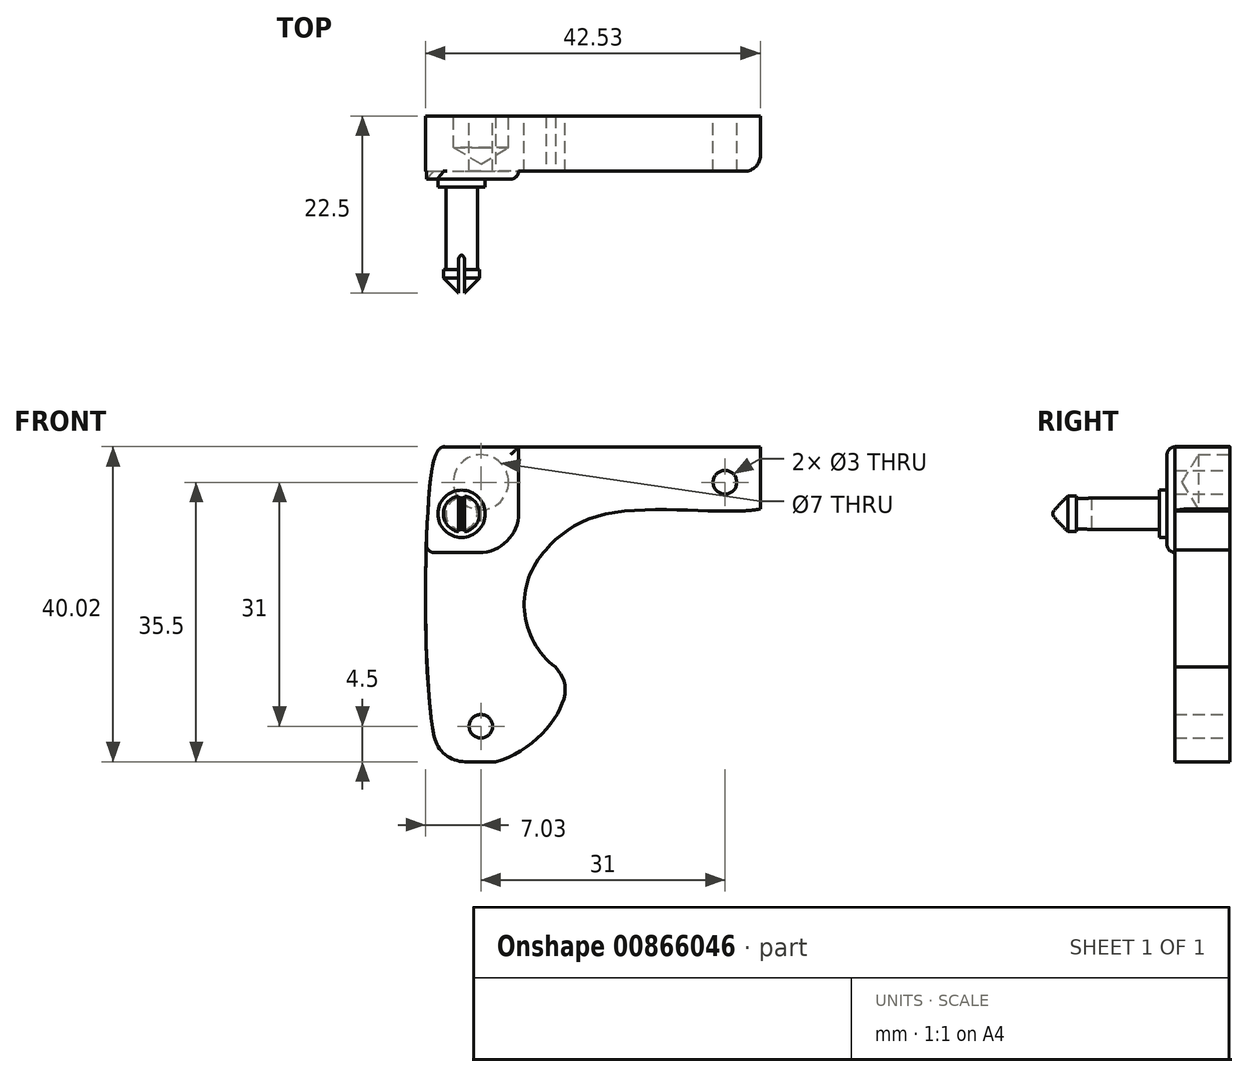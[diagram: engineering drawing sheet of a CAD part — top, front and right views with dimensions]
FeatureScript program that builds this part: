
annotation { "Feature Type Name" : "Feature", "Feature Type Description" : "" }
export const myFeature = defineFeature(function(context is Context, id is Id, definition is map)
    precondition{}
    {
        {
            var Q0;
            Q0=qCreatedBy(makeId("Front.planeOp"),FACE);
            var sketch = newSketch(context, id + "F0", { "sketchPlane" : qUnion([Q0])});
            skLineSegment(sketch, "E0.bottom", {"start": v(-20, 20) * mm, "end": v(20, 20) * mm});
            skLineSegment(sketch, "E0.top", {"start": v(-20, -20) * mm, "end": v(20, -20) * mm});
            skLineSegment(sketch, "E0.left", {"start": v(-20, 20) * mm, "end": v(-20, -20) * mm});
            skLineSegment(sketch, "E0.right", {"start": v(20, 20) * mm, "end": v(20, -20) * mm});
            skPoint(sketch, "E1", {"position": v(-15.5, 15.5) * mm});
            skPoint(sketch, "E2", {"position": v(15.5, 15.5) * mm});
            skPoint(sketch, "E3", {"position": v(15.5, -15.5) * mm});
            skPoint(sketch, "E4", {"position": v(-15.5, -15.5) * mm});
            skPoint(sketch, "E5", {"position": v(0, 0) * mm});
            skFitSpline(sketch, "E6", {"points": [v(-20, 20) * mm, v(-22.22, 12.2) * mm, v(-20, -20) * mm, v(-13.87, 3.79) * mm, v(-20, 20) * mm]});
            skSolve(sketch);
        }
        {
            var Q0;
            Q0=makeQuery(id+"F0.imprint","IMPRINT",FACE,{"disambiguationData":[TD([[makeQuery(id+"F0.imprint","IMPRINT",EDGE,{"derivedFrom":sQuery(id+"F0.wireOp",EDGE,"E0.bottom")}),-1.0]])]});
            var Q1;
            {var subQ1=sQuery(id+"F0.wireOp",EDGE,"E0.left");Q1=makeQuery(id+"F0.imprint","IMPRINT",FACE,{"disambiguationData":[TD([[makeQuery(id+"F0.imprint","IMPRINT",EDGE,{"derivedFrom":subQ1}),1.0]])]});}
            var Q2;
            {var subQ0=sQuery(id+"F0.wireOp",EDGE,"E0.left");Q2=makeQuery(id+"F0.imprint","IMPRINT",FACE,{"disambiguationData":[TD([[makeQuery(id+"F0.imprint","IMPRINT",EDGE,{"derivedFrom":subQ0}),-1.0]])]});}
            extrude(context, id + "F1", {"entities" : qUnion([Q0, Q1, Q2]), "depth" : 7 * mm, "offsetDistance" : 25 * mm});
        }
        {
            var Q0;
            Q0=sQuery(id+"F0.wireOp",VERTEX,"E5");
            var Q1;
            Q1=makeQuery(id+"F1.opExtrude","SWEPT_BODY",BODY,{"disambiguationData":[OSD([sQuery(id+"F0.wireOp",EDGE,"E0.bottom"),sQuery(id+"F0.wireOp",EDGE,"E0.top"),sQuery(id+"F0.wireOp",EDGE,"E0.left"),sQuery(id+"F0.wireOp",EDGE,"E0.right")])]});
            hole(context, id + "F2", {"style" : HoleStyle.SIMPLE, "endStyle" : HoleEndStyle.THROUGH, "oppositeDirection" : true, "holeDiameter" : 20 * mm, "majorDiameter" : 5 * mm, "isTappedThrough" : true, "tappedDepth" : 12 * mm, "tapClearance" : 3, "locations" : qUnion([Q0]), "scope" : qUnion([Q1])});
        }
        {
            var Q0;
            Q0=sQuery(id+"F0.wireOp",VERTEX,"E2");
            var Q1;
            Q1=sQuery(id+"F0.wireOp",VERTEX,"E3");
            var Q2;
            Q2=sQuery(id+"F0.wireOp",VERTEX,"E4");
            var Q3;
            Q3=makeQuery(id+"F1.opExtrude","SWEPT_BODY",BODY,{"disambiguationData":[OSD([sQuery(id+"F0.wireOp",EDGE,"E0.bottom"),sQuery(id+"F0.wireOp",EDGE,"E0.top"),sQuery(id+"F0.wireOp",EDGE,"E0.left"),sQuery(id+"F0.wireOp",EDGE,"E0.right")])]});
            hole(context, id + "F3", {"style" : HoleStyle.SIMPLE, "endStyle" : HoleEndStyle.THROUGH, "oppositeDirection" : true, "holeDiameter" : 3 * mm, "majorDiameter" : 5 * mm, "isTappedThrough" : true, "tappedDepth" : 12 * mm, "tapClearance" : 3, "locations" : qUnion([Q0, Q1, Q2]), "scope" : qUnion([Q3])});
        }
        {
            var Q0;
            Q0=sQuery(id+"F0.wireOp",VERTEX,"E1");
            var Q1;
            Q1=makeQuery(id+"F1.opExtrude","SWEPT_BODY",BODY,{"disambiguationData":[OSD([sQuery(id+"F0.wireOp",EDGE,"E0.bottom"),sQuery(id+"F0.wireOp",EDGE,"E0.top"),sQuery(id+"F0.wireOp",EDGE,"E0.left"),sQuery(id+"F0.wireOp",EDGE,"E0.right")])]});
            hole(context, id + "F4", {"style" : HoleStyle.SIMPLE, "endStyle" : HoleEndStyle.BLIND, "oppositeDirection" : true, "holeDiameter" : 7 * mm, "majorDiameter" : 5 * mm, "holeDepth" : 4 * mm, "isTappedThrough" : true, "tappedDepth" : 12 * mm, "tapClearance" : 3, "locations" : qUnion([Q0]), "scope" : qUnion([Q1])});
        }
        {
            var Q0;
            Q0=qCreatedBy(makeId("Front.planeOp"),FACE);
            var sketch = newSketch(context, id + "F5", { "sketchPlane" : qUnion([Q0])});
            skLineSegment(sketch, "E7", {"start": v(0, 6.5) * mm, "end": v(-44.68, 6.5) * mm});
            skCircle(sketch, "E8", {"center": v(0, 0) * mm, "radius": 6.5 * mm});
            skSolve(sketch);
        }
        {
            var Q0;
            Q0=makeQuery(id+"F1.opExtrude","CAP_FACE",FACE,{"disambiguationData":[OSD([sQuery(id+"F0.wireOp",EDGE,"E0.bottom"),sQuery(id+"F0.wireOp",EDGE,"E0.top"),sQuery(id+"F0.wireOp",EDGE,"E0.left"),sQuery(id+"F0.wireOp",EDGE,"E0.right")])],"isStart":false});
            var sketch = newSketch(context, id + "F6", { "sketchPlane" : qUnion([Q0])});
            skLineSegment(sketch, "E9.bottom", {"start": v(-23.6, 20) * mm, "end": v(-10.72, 20) * mm});
            skLineSegment(sketch, "E9.top", {"start": v(-23.6, 6.57) * mm, "end": v(-10.72, 6.57) * mm});
            skLineSegment(sketch, "E9.left", {"start": v(-23.6, 20) * mm, "end": v(-23.6, 6.57) * mm});
            skLineSegment(sketch, "E9.right", {"start": v(-10.72, 20) * mm, "end": v(-10.72, 6.57) * mm});
            skSolve(sketch);
        }
        {
            var Q0;
            Q0=makeQuery(id+"F6.imprint","IMPRINT",FACE,{"disambiguationData":[TD([[makeQuery(id+"F6.imprint","IMPRINT",EDGE,{"derivedFrom":sQuery(id+"F6.wireOp",EDGE,"E9.bottom")}),-1.0]])]});
            extrude(context, id + "F7", {"entities" : qUnion([Q0]), "operationType" : NewBodyOperationType.ADD, "depth" : 1 * mm, "offsetDistance" : 25 * mm});
        }
        {
            var Q0;
            Q0=makeQuery(id+"F7.opExtrude","CAP_FACE",FACE,{"disambiguationData":[OSD([sQuery(id+"F6.wireOp",EDGE,"E9.bottom"),sQuery(id+"F6.wireOp",EDGE,"E9.top"),sQuery(id+"F6.wireOp",EDGE,"E9.left"),sQuery(id+"F6.wireOp",EDGE,"E9.right")])],"isStart":false});
            var sketch = newSketch(context, id + "F8", { "sketchPlane" : qUnion([Q0])});
            skCircle(sketch, "E10", {"center": v(-17.96, 11.5) * mm, "radius": 3 * mm});
            skSolve(sketch);
        }
        {
            var Q0;
            Q0=makeQuery(id+"F8.imprint","IMPRINT",FACE,{"disambiguationData":[TD([[makeQuery(id+"F8.imprint","IMPRINT",EDGE,{"derivedFrom":sQuery(id+"F8.wireOp",EDGE,"E10")}),1.0]])]});
            extrude(context, id + "F9", {"entities" : qUnion([Q0]), "operationType" : NewBodyOperationType.ADD, "depth" : 1 * mm, "offsetDistance" : 25 * mm});
        }
        {
            var Q0;
            Q0=makeQuery(id+"F9.opExtrude","CAP_FACE",FACE,{"disambiguationData":[OSD([sQuery(id+"F6.wireOp",EDGE,"E9.top"),sQuery(id+"F8.wireOp",EDGE,"E10")])],"isStart":false});
            var sketch = newSketch(context, id + "F10", { "sketchPlane" : qUnion([Q0])});
            skCircle(sketch, "E11", {"center": v(-17.96, 11.5) * mm, "radius": 2 * mm});
            skSolve(sketch);
        }
        {
            var Q0;
            Q0=makeQuery(id+"F10.imprint","IMPRINT",FACE,{"disambiguationData":[TD([[makeQuery(id+"F10.imprint","IMPRINT",EDGE,{"derivedFrom":sQuery(id+"F10.wireOp",EDGE,"E11")}),1.0]])]});
            extrude(context, id + "F11", {"entities" : qUnion([Q0]), "operationType" : NewBodyOperationType.ADD, "depth" : 10.5 * mm, "offsetDistance" : 25 * mm});
        }
        {
            var Q0;
            Q0=makeQuery(id+"F11.opExtrude","CAP_FACE",FACE,{"disambiguationData":[OSD([sQuery(id+"F10.wireOp",EDGE,"E11")])],"isStart":false});
            var sketch = newSketch(context, id + "F12", { "sketchPlane" : qUnion([Q0])});
            skCircle(sketch, "E12", {"center": v(-17.96, 11.5) * mm, "radius": 2.3 * mm});
            skSolve(sketch);
        }
        {
            var Q0;
            Q0=makeQuery(id+"F12.imprint","IMPRINT",FACE,{"disambiguationData":[TD([[makeQuery(id+"F12.imprint","IMPRINT",EDGE,{"derivedFrom":makeQuery(id+"F11.opExtrude","CAP_EDGE",EDGE,{"disambiguationData":[OSD([sQuery(id+"F10.wireOp",EDGE,"E11")])],"isStart":false})}),1.0]])]});
            var Q1;
            Q1=makeQuery(id+"F12.imprint","IMPRINT",FACE,{"disambiguationData":[TD([[makeQuery(id+"F12.imprint","IMPRINT",EDGE,{"derivedFrom":sQuery(id+"F12.wireOp",EDGE,"E12")}),1.0]])]});
            extrude(context, id + "F13", {"entities" : qUnion([Q0, Q1]), "operationType" : NewBodyOperationType.ADD, "depth" : 3 * mm, "offsetDistance" : 25 * mm});
        }
        {
            var Q0;
            Q0=makeQuery(id+"F13.opExtrude","CAP_FACE",FACE,{"disambiguationData":[OSD([sQuery(id+"F12.wireOp",EDGE,"E12")])],"isStart":false});
            var sketch = newSketch(context, id + "F14", { "sketchPlane" : qUnion([Q0])});
            skLineSegment(sketch, "E13.bottom", {"start": v(-17.56, 9.13) * mm, "end": v(-18.36, 9.13) * mm});
            skLineSegment(sketch, "E13.top", {"start": v(-17.56, 13.87) * mm, "end": v(-18.36, 13.87) * mm});
            skLineSegment(sketch, "E13.left", {"start": v(-17.56, 9.13) * mm, "end": v(-17.56, 13.87) * mm});
            skLineSegment(sketch, "E13.right", {"start": v(-18.36, 9.13) * mm, "end": v(-18.36, 13.87) * mm});
            skPoint(sketch, "E13.middle", {"position": v(-17.96, 11.5) * mm});
            skSolve(sketch);
        }
        {
            var Q0;
            {var subQ0=sQuery(id+"F14.wireOp",EDGE,"E13.top");Q0=makeQuery(id+"F14.imprint","IMPRINT",FACE,{"disambiguationData":[TD([[makeQuery(id+"F14.imprint","IMPRINT",EDGE,{"derivedFrom":subQ0}),1.0]])]});}
            var Q1;
            {var subQ0=sQuery(id+"F14.wireOp",EDGE,"E13.left");var subQ1=makeQuery(id+"F13.opExtrude","CAP_EDGE",EDGE,{"disambiguationData":[OSD([sQuery(id+"F12.wireOp",EDGE,"E12")])],"isStart":false});var subQ2=makeQuery(id+"F14.imprint","INTERSECT",VERTEX,{"disambiguationData":[OD(0.0)],"derivedFrom":[subQ1,subQ0]});Q1=makeQuery(id+"F14.imprint","IMPRINT",FACE,{"disambiguationData":[TD([[makeQuery(id+"F14.imprint","IMPRINT",EDGE,{"disambiguationData":[TD([[subQ2,-1.0]])],"derivedFrom":subQ0}),1.0]])]});}
            var Q2;
            {var subQ0=sQuery(id+"F14.wireOp",EDGE,"E13.bottom");Q2=makeQuery(id+"F14.imprint","IMPRINT",FACE,{"disambiguationData":[TD([[makeQuery(id+"F14.imprint","IMPRINT",EDGE,{"derivedFrom":subQ0}),-1.0]])]});}
            extrude(context, id + "F15", {"entities" : qUnion([Q0, Q1, Q2]), "operationType" : NewBodyOperationType.REMOVE, "oppositeDirection" : true, "depth" : 5 * mm, "offsetDistance" : 25 * mm});
        }
        {
            var Q0;
            {var subQ0=sQuery(id+"F12.wireOp",EDGE,"E12");Q0=makeQuery(id+"F15.boolean.opBoolean","SPLIT",EDGE,{"disambiguationData":[TD([makeQuery(id+"F15.opExtrude","SWEPT_FACE",FACE,{"disambiguationData":[OSD([sQuery(id+"F14.wireOp",EDGE,"E13.right")])]})])],"derivedFrom":makeQuery(id+"F13.opExtrude","CAP_EDGE",EDGE,{"disambiguationData":[OSD([subQ0])],"isStart":false})});}
            var Q1;
            {var subQ0=sQuery(id+"F12.wireOp",EDGE,"E12");Q1=makeQuery(id+"F15.boolean.opBoolean","SPLIT",EDGE,{"disambiguationData":[TD([makeQuery(id+"F15.opExtrude","SWEPT_FACE",FACE,{"disambiguationData":[OSD([sQuery(id+"F14.wireOp",EDGE,"E13.left")])]})])],"derivedFrom":makeQuery(id+"F13.opExtrude","CAP_EDGE",EDGE,{"disambiguationData":[OSD([subQ0])],"isStart":false})});}
            chamfer(context, id + "F16", {"entities" : qUnion([Q0, Q1]), "width" : 1.9 * mm, "tangentPropagation" : true});
        }
        {
            var Q0;
            {var subQ7=sQuery(id+"F6.wireOp",EDGE,"E9.top");Q0=makeQuery(id+"F6.imprint","IMPRINT",FACE,{"disambiguationData":[TD([[makeQuery(id+"F6.imprint","IMPRINT",EDGE,{"derivedFrom":subQ7}),-1.0]])]});}
            var sketch = newSketch(context, id + "F17", { "sketchPlane" : qUnion([Q0])});
            skFitSpline(sketch, "E14", {"points": [v(22.15, 16.76) * mm, v(21.52, 12.68) * mm, v(0, 11.37) * mm, v(-9.58, 2.55) * mm, v(-8.96, -4.93) * mm, v(-4.8, -10.46) * mm, v(-13.92, -20.06) * mm, v(-22.03, -19.9) * mm, v(13.8, -32.16) * mm, v(31.86, -14) * mm, v(30.6, 5.78) * mm, v(27.78, 17.76) * mm, v(23.51, 20.4) * mm, v(21.16, 19.76) * mm, v(22.15, 16.76) * mm]});
            skSolve(sketch);
        }
        {
            var Q0;
            {var subQ0=sQuery(id+"F17.wireOp",EDGE,"E14");var subQ1=makeQuery(id+"F6.imprint","IMPRINT",EDGE,{"derivedFrom":makeQuery(id+"F1.opExtrude","CAP_EDGE",EDGE,{"disambiguationData":[OSD([sQuery(id+"F0.wireOp",EDGE,"E0.right")])],"isStart":false})});var subQ2=makeQuery(id+"F17.imprint","INTERSECT",VERTEX,{"derivedFrom":[subQ1,subQ0]});Q0=makeQuery(id+"F17.imprint","IMPRINT",FACE,{"disambiguationData":[TD([[makeQuery(id+"F17.imprint","IMPRINT",EDGE,{"disambiguationData":[TD([[subQ2,1.0]])],"derivedFrom":subQ0}),1.0]])]});}
            var Q1;
            {var subQ0=sQuery(id+"F0.wireOp",EDGE,"E0.right");var subQ1=sQuery(id+"F0.wireOp",EDGE,"E0.top");var subQ3=makeQuery(id+"F6.imprint","IMPRINT",EDGE,{"derivedFrom":makeQuery(id+"F1.opExtrude","CAP_EDGE",EDGE,{"disambiguationData":[OSD([subQ0])],"isStart":false})});var subQ4=makeQuery(id+"F6.imprint","IMPRINT",EDGE,{"derivedFrom":makeQuery(id+"F1.opExtrude","CAP_EDGE",EDGE,{"disambiguationData":[OSD([subQ1])],"isStart":false})});var subQ5=makeQuery(id+"F17.imprint","INTERSECT",VERTEX,{"derivedFrom":[subQ4,subQ3]});Q1=makeQuery(id+"F17.imprint","IMPRINT",FACE,{"disambiguationData":[TD([[makeQuery(id+"F17.imprint","IMPRINT",EDGE,{"disambiguationData":[TD([[subQ5,1.0]])],"derivedFrom":subQ4}),1.0]])]});}
            extrude(context, id + "F18", {"entities" : qUnion([Q0, Q1]), "operationType" : NewBodyOperationType.REMOVE, "oppositeDirection" : true, "depth" : 25 * mm, "offsetDistance" : 25 * mm});
        }
        {
            var Q0;
            Q0=makeQuery(id+"F7.opExtrude","SWEPT_EDGE",EDGE,{"disambiguationData":[OSD([sQuery(id+"F6.wireOp",EDGE,"E9.top"),sQuery(id+"F6.wireOp",EDGE,"E9.right")])]});
            fillet(context, id + "F19", {"entities" : qUnion([Q0]), "radius" : 5 * mm, "tangentPropagation" : true, "allowEdgeOverflow" : false});
        }
        {
            var Q0;
            Q0=makeQuery(id+"F7.opExtrude","CAP_EDGE",EDGE,{"disambiguationData":[OSD([sQuery(id+"F6.wireOp",EDGE,"E9.top")])],"isStart":false});
            var Q1;
            {var subQ0=sQuery(id+"F6.wireOp",EDGE,"E9.right");var subQ1=sQuery(id+"F6.wireOp",EDGE,"E9.top");Q1=makeQuery(id+"F19.opFillet","BLEND_EDGE",EDGE,{"blendedFrom":[makeQuery(id+"F7.opExtrude","SWEPT_EDGE",EDGE,{"disambiguationData":[OSD([subQ1,subQ0])]}),makeQuery(id+"F7.opExtrude","CAP_FACE",FACE,{"disambiguationData":[OSD([sQuery(id+"F0.wireOp",EDGE,"E0.bottom"),sQuery(id+"F0.wireOp",EDGE,"E0.top"),sQuery(id+"F0.wireOp",EDGE,"E0.left"),sQuery(id+"F0.wireOp",EDGE,"E0.right"),sQuery(id+"F3.hole-0.sketch.wireOp",EDGE,"core_line_2"),sQuery(id+"F6.wireOp",EDGE,"E9.bottom"),subQ1,sQuery(id+"F6.wireOp",EDGE,"E9.left"),subQ0])],"isStart":false})],"blendedInto":[makeQuery(id+"F7.opExtrude","CAP_FACE",FACE,{"disambiguationData":[OSD([sQuery(id+"F0.wireOp",EDGE,"E0.bottom"),sQuery(id+"F0.wireOp",EDGE,"E0.top"),sQuery(id+"F0.wireOp",EDGE,"E0.left"),sQuery(id+"F0.wireOp",EDGE,"E0.right"),sQuery(id+"F3.hole-0.sketch.wireOp",EDGE,"core_line_2"),sQuery(id+"F6.wireOp",EDGE,"E9.bottom"),subQ1,sQuery(id+"F6.wireOp",EDGE,"E9.left"),subQ0])],"isStart":false})]});}
            var Q2;
            Q2=makeQuery(id+"F7.opExtrude","CAP_EDGE",EDGE,{"disambiguationData":[OSD([sQuery(id+"F6.wireOp",EDGE,"E9.bottom")])],"isStart":false});
            var Q3;
            Q3=makeQuery(id+"F7.opExtrude","SWEPT_EDGE",EDGE,{"disambiguationData":[OSD([sQuery(id+"F0.wireOp",EDGE,"E6"),sQuery(id+"F6.wireOp",EDGE,"E9.top")])]});
            fillet(context, id + "F20", {"entities" : qUnion([Q0, Q1, Q2, Q3]), "radius" : 1 * mm, "tangentPropagation" : true, "allowEdgeOverflow" : false});
        }
        {
            var Q0;
            Q0=makeQuery(id+"F2.hole-0.boolean.opBoolean","INTERSECT",EDGE,{"derivedFrom":[makeQuery(id+"F1.opExtrude","CAP_FACE",FACE,{"disambiguationData":[OSD([sQuery(id+"F0.wireOp",EDGE,"E0.bottom"),sQuery(id+"F0.wireOp",EDGE,"E0.top"),sQuery(id+"F0.wireOp",EDGE,"E0.left"),sQuery(id+"F0.wireOp",EDGE,"E0.right")])],"isStart":false}),makeQuery(id+"F2.hole-0.opRevolve","SWEPT_FACE",FACE,{"disambiguationData":[OSD([sQuery(id+"F2.hole-0.sketch.wireOp",EDGE,"core_line_2")])]})]});
            var Q1;
            {var subQ0=sQuery(id+"F0.wireOp",EDGE,"E0.right");var subQ1=sQuery(id+"F17.wireOp",EDGE,"E14");Q1=makeQuery(id+"F18.boolean.opBoolean","COPY",EDGE,{"disambiguationData":[TD([makeQuery(id+"F1.opExtrude","SWEPT_FACE",FACE,{"disambiguationData":[OSD([subQ0])]})])],"derivedFrom":makeQuery(id+"F18.opExtrude","CAP_EDGE",EDGE,{"disambiguationData":[OSD([subQ1])],"isStart":true})});}
            var Q2;
            {var subQ0=sQuery(id+"F0.wireOp",EDGE,"E0.top");var subQ1=sQuery(id+"F17.wireOp",EDGE,"E14");Q2=makeQuery(id+"F18.boolean.opBoolean","COPY",EDGE,{"disambiguationData":[TD([makeQuery(id+"F1.opExtrude","SWEPT_FACE",FACE,{"disambiguationData":[OSD([subQ0])]})])],"derivedFrom":makeQuery(id+"F18.opExtrude","CAP_EDGE",EDGE,{"disambiguationData":[OSD([subQ1])],"isStart":true})});}
            var Q3;
            Q3=makeQuery(id+"F1.opExtrude","CAP_EDGE",EDGE,{"disambiguationData":[OSD([sQuery(id+"F0.wireOp",EDGE,"E0.right")])],"isStart":false});
            fillet(context, id + "F21", {"entities" : qUnion([Q0, Q1, Q2, Q3]), "radius" : 2 * mm, "tangentPropagation" : true, "allowEdgeOverflow" : false});
        }
        {
            var Q0;
            Q0=makeQuery(id+"F15.boolean.opBoolean","COPY",EDGE,{"derivedFrom":makeQuery(id+"F15.opExtrude","CAP_EDGE",EDGE,{"disambiguationData":[OSD([sQuery(id+"F14.wireOp",EDGE,"E13.right")])],"isStart":false})});
            var Q1;
            Q1=makeQuery(id+"F15.boolean.opBoolean","COPY",EDGE,{"derivedFrom":makeQuery(id+"F15.opExtrude","CAP_EDGE",EDGE,{"disambiguationData":[OSD([sQuery(id+"F14.wireOp",EDGE,"E13.left")])],"isStart":false})});
            fillet(context, id + "F22", {"entities" : qUnion([Q0, Q1]), "radius" : 0.8 * mm, "tangentPropagation" : true, "allowEdgeOverflow" : false});
        }
        {
            var Q0;
            Q0=makeQuery(id+"F7.boolean.opBoolean","MERGE",EDGE,{"derivedFrom":[makeQuery(id+"F1.opExtrude","SWEPT_EDGE",EDGE,{"disambiguationData":[OSD([sQuery(id+"F0.wireOp",EDGE,"E0.bottom"),sQuery(id+"F0.wireOp",EDGE,"E0.left")])]}),makeQuery(id+"F7.opExtrude","SWEPT_EDGE",EDGE,{"disambiguationData":[OSD([sQuery(id+"F6.wireOp",EDGE,"E9.bottom"),sQuery(id+"F6.wireOp",EDGE,"E9.left")])]})]});
            var Q1;
            Q1=makeQuery(id+"F1.opExtrude","SWEPT_EDGE",EDGE,{"disambiguationData":[OSD([sQuery(id+"F0.wireOp",EDGE,"E0.top"),sQuery(id+"F0.wireOp",EDGE,"E0.left")])]});
            fillet(context, id + "F23", {"entities" : qUnion([Q0, Q1]), "radius" : 4 * mm, "tangentPropagation" : true, "allowEdgeOverflow" : false});
        }
    });
